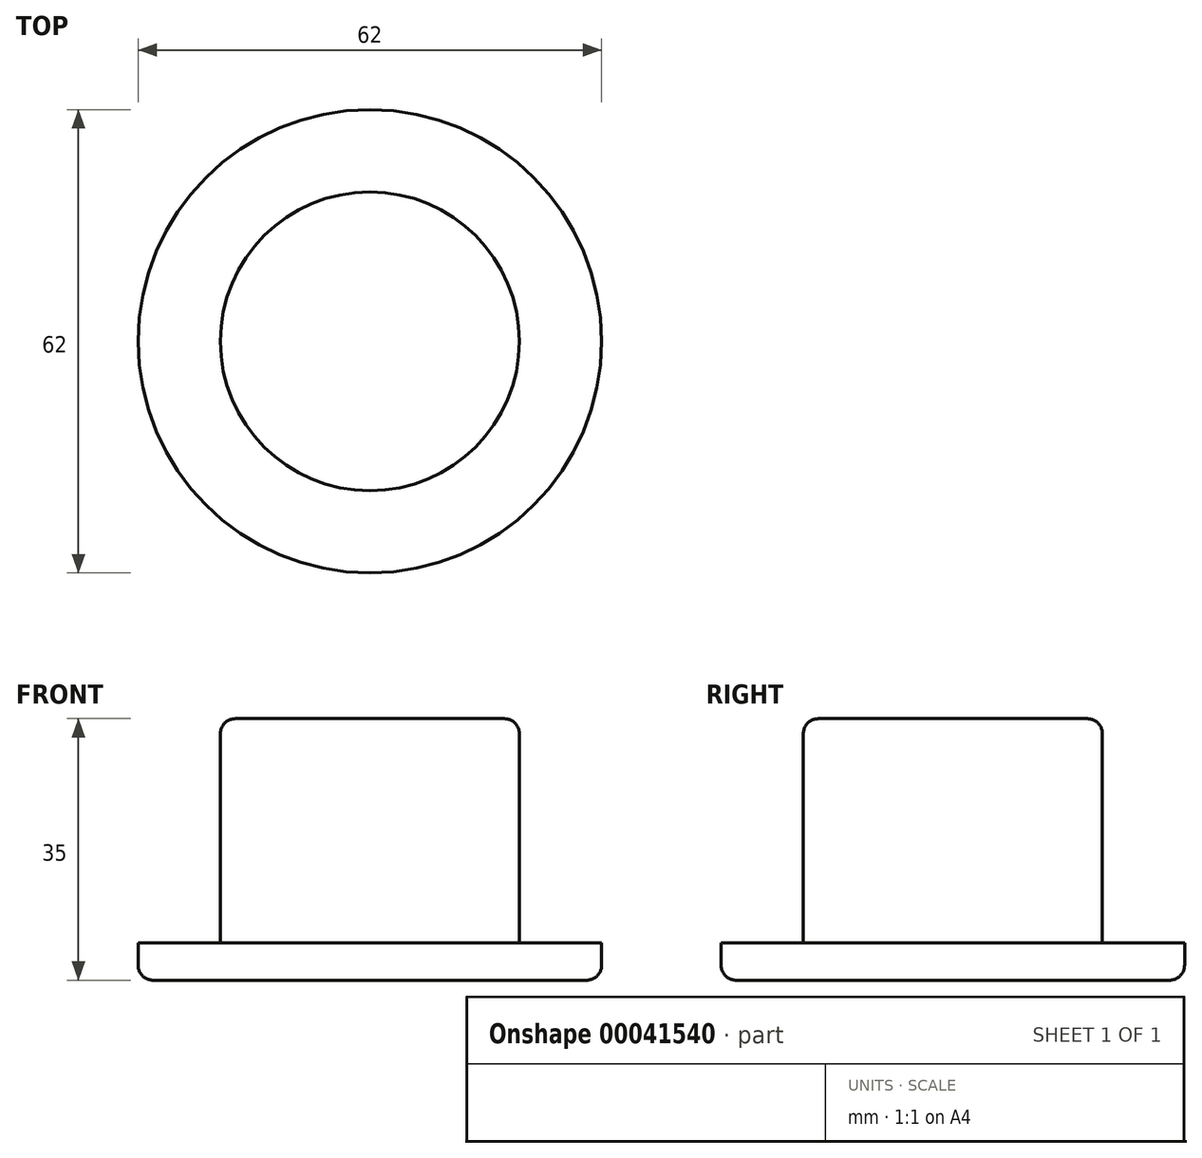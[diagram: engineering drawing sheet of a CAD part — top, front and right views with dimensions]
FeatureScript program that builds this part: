
annotation { "Feature Type Name" : "Feature", "Feature Type Description" : "" }
export const myFeature = defineFeature(function(context is Context, id is Id, definition is map)
    precondition{}
    {
        {
            var Q0;
            Q0=qCreatedBy(makeId("Top.planeOp"),FACE);
            var sketch = newSketch(context, id + "F0", { "sketchPlane" : qUnion([Q0])});
            skCircle(sketch, "E0", {"center": v(0, 0) * mm, "radius": 31 * mm});
            skSolve(sketch);
        }
        {
            var Q0;
            Q0=makeQuery(id+"F0.imprint","IMPRINT",FACE,{"disambiguationData":[TD([[makeQuery(id+"F0.imprint","IMPRINT",EDGE,{"derivedFrom":sQuery(id+"F0.wireOp",EDGE,"E0")}),1.0]])]});
            extrude(context, id + "F1", {"entities" : qUnion([Q0]), "depth" : 5 * mm});
        }
        {
            var Q0;
            Q0=makeQuery(id+"F1.opExtrude","CAP_FACE",FACE,{"disambiguationData":[OSD([sQuery(id+"F0.wireOp",EDGE,"E0")])],"isStart":false});
            var sketch = newSketch(context, id + "F2", { "sketchPlane" : qUnion([Q0])});
            skCircle(sketch, "E1", {"center": v(0, 0) * mm, "radius": 20 * mm});
            skSolve(sketch);
        }
        {
            var Q0;
            Q0=makeQuery(id+"F2.imprint","IMPRINT",FACE,{"disambiguationData":[TD([[makeQuery(id+"F2.imprint","IMPRINT",EDGE,{"derivedFrom":sQuery(id+"F2.wireOp",EDGE,"E1")}),1.0]])]});
            extrude(context, id + "F3", {"entities" : qUnion([Q0]), "operationType" : NewBodyOperationType.ADD, "depth" : 30 * mm});
        }
        {
            var Q0;
            Q0=makeQuery(id+"F3.opExtrude","CAP_FACE",FACE,{"disambiguationData":[OSD([sQuery(id+"F2.wireOp",EDGE,"E1")])],"isStart":false});
            var Q1;
            Q1=makeQuery(id+"F3.opExtrude","CAP_EDGE",EDGE,{"disambiguationData":[OSD([sQuery(id+"F2.wireOp",EDGE,"E1")])],"isStart":true});
            var Q2;
            Q2=makeQuery(id+"F1.opExtrude","CAP_EDGE",EDGE,{"disambiguationData":[OSD([sQuery(id+"F0.wireOp",EDGE,"E0")])],"isStart":true});
            fillet(context, id + "F4", {"entities" : qUnion([Q0, Q1, Q2]), "radius" : 2 * mm, "tangentPropagation" : true, "allowEdgeOverflow" : false});
        }
    });
